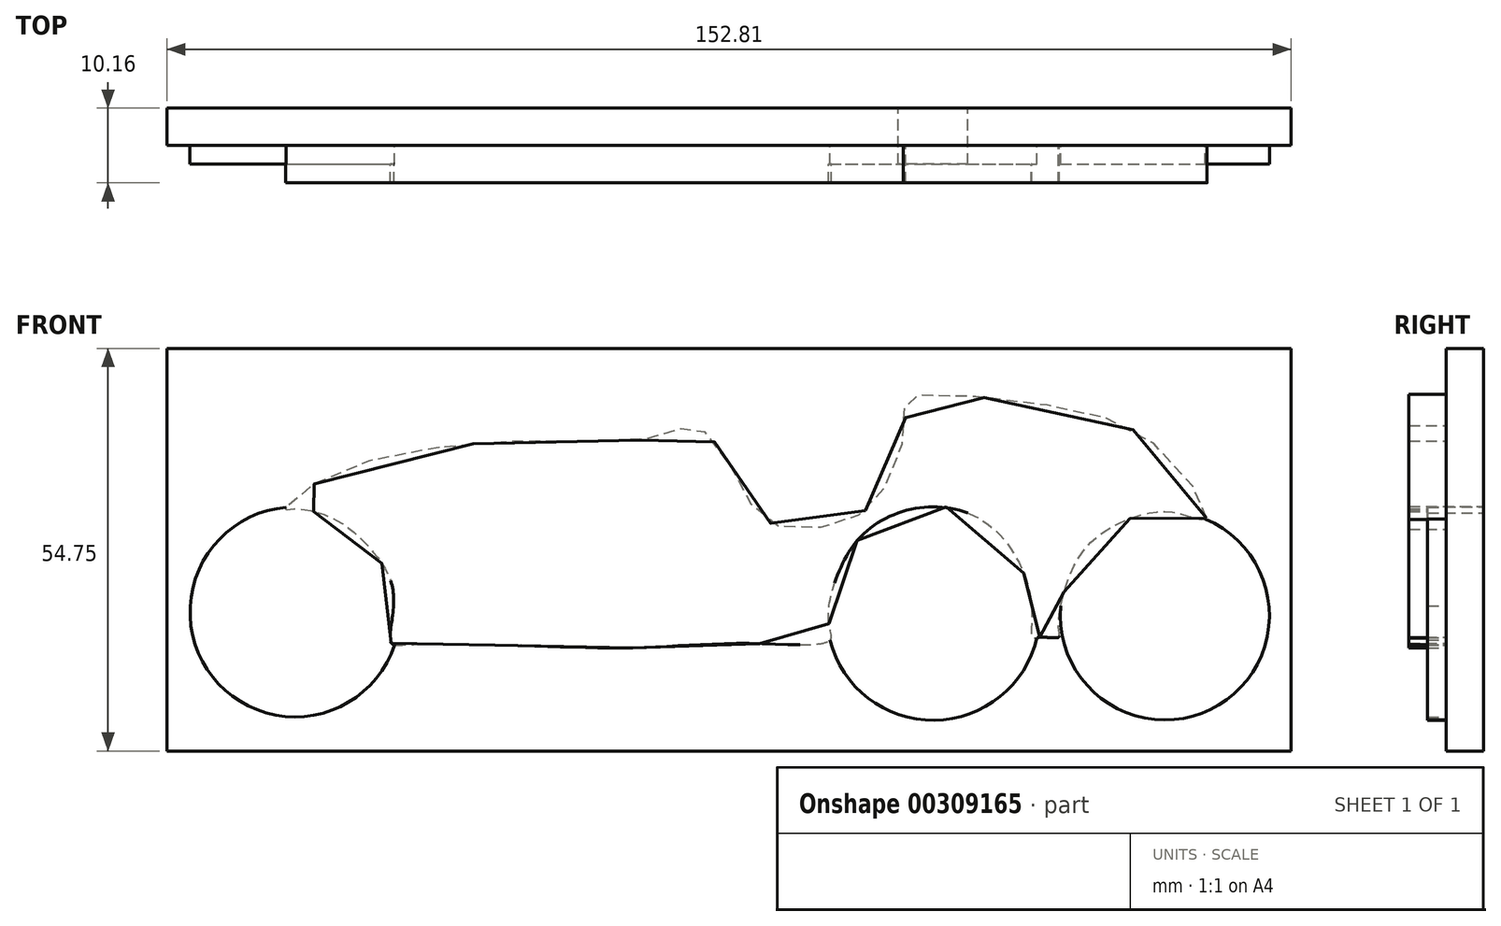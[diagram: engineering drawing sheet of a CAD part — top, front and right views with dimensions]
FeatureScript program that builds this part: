
annotation { "Feature Type Name" : "Feature", "Feature Type Description" : "" }
export const myFeature = defineFeature(function(context is Context, id is Id, definition is map)
    precondition{}
    {
        {
            var Q0;
            Q0=qCreatedBy(makeId("Front.planeOp"),FACE);
            var sketch = newSketch(context, id + "F0", { "sketchPlane" : qUnion([Q0])});
            skFitSpline(sketch, "E0", {"points": [v(91.57, -9.24) * mm, v(85.46, 0) * mm, v(68.77, 6.28) * mm, v(50.67, 6.98) * mm, v(50.67, 4.63) * mm, v(47.6, -5.48) * mm, v(41.73, -9.95) * mm, v(32.33, -9.95) * mm, v(27.86, -3.83) * mm, v(22.22, 3.22) * mm, v(18.22, 2.04) * mm, v(-1.62, 1.2) * mm, v(-28.2, -3.75) * mm, v(-33.55, -8) * mm, v(-32.54, -8) * mm, v(-27.09, -9.3) * mm, v(-21.67, -13.85) * mm, v(-18.88, -19.98) * mm, v(-19.29, -26.1) * mm, v(-17.52, -26.47) * mm, v(-2.12, -26.56) * mm, v(14.58, -26.84) * mm, v(29.22, -26.28) * mm, v(40.42, -25.81) * mm, v(40.25, -23.5) * mm, v(41.6, -16.58) * mm, v(46.02, -10.5) * mm, v(54.62, -7.63) * mm, v(63.21, -11.21) * mm, v(67.8, -21.06) * mm, v(67.9, -25.5) * mm, v(68.97, -25.44) * mm, v(71.49, -25.44) * mm, v(71.49, -24.23) * mm, v(74.15, -14.72) * mm, v(80.72, -9.47) * mm, v(87.4, -8.51) * mm, v(91.57, -9.24) * mm]});
            skSolve(sketch);
        }
        {
            var Q0;
            Q0=makeQuery(id+"F0.imprint","IMPRINT",FACE,{"disambiguationData":[TD([[makeQuery(id+"F0.imprint","IMPRINT",EDGE,{"derivedFrom":sQuery(id+"F0.wireOp",EDGE,"E0")}),1.0]])]});
            extrude(context, id + "F1", {"entities" : qUnion([Q0]), "depth" : 5.08 * mm});
        }
        {
            var Q0;
            Q0=qCreatedBy(makeId("Front.planeOp"),FACE);
            var sketch = newSketch(context, id + "F2", { "sketchPlane" : qUnion([Q0])});
            skCircle(sketch, "E1", {"center": v(-32.3, -21.99) * mm, "radius": 14.27 * mm});
            skCircle(sketch, "E2", {"center": v(54.43, -22.22) * mm, "radius": 14.5 * mm});
            skCircle(sketch, "E3", {"center": v(85.92, -22.47) * mm, "radius": 14.21 * mm});
            skSolve(sketch);
        }
        {
            var Q0;
            Q0=makeQuery(id+"F2.imprint","IMPRINT",FACE,{"disambiguationData":[TD([[makeQuery(id+"F2.imprint","IMPRINT",EDGE,{"derivedFrom":sQuery(id+"F2.wireOp",EDGE,"E1")}),1.0]])]});
            var Q1;
            Q1=makeQuery(id+"F2.imprint","IMPRINT",FACE,{"disambiguationData":[TD([[makeQuery(id+"F2.imprint","IMPRINT",EDGE,{"derivedFrom":sQuery(id+"F2.wireOp",EDGE,"E2")}),1.0]])]});
            var Q2;
            Q2=makeQuery(id+"F2.imprint","IMPRINT",FACE,{"disambiguationData":[TD([[makeQuery(id+"F2.imprint","IMPRINT",EDGE,{"derivedFrom":sQuery(id+"F2.wireOp",EDGE,"E3")}),1.0]])]});
            extrude(context, id + "F3", {"entities" : qUnion([Q0, Q1, Q2]), "operationType" : NewBodyOperationType.ADD, "depth" : 2.54 * mm});
        }
        {
            var Q0;
            Q0=makeQuery(id+"F3.boolean.opBoolean","MERGE",FACE,{"derivedFrom":[makeQuery(id+"F1.opExtrude","CAP_FACE",FACE,{"disambiguationData":[OSD([sQuery(id+"F0.wireOp",EDGE,"E0")])],"isStart":true}),makeQuery(id+"F3.opExtrude","CAP_FACE",FACE,{"disambiguationData":[OSD([sQuery(id+"F2.wireOp",EDGE,"E1")])],"isStart":true}),makeQuery(id+"F3.opExtrude","CAP_FACE",FACE,{"disambiguationData":[OSD([sQuery(id+"F2.wireOp",EDGE,"E2")])],"isStart":true}),makeQuery(id+"F3.opExtrude","CAP_FACE",FACE,{"disambiguationData":[OSD([sQuery(id+"F2.wireOp",EDGE,"E3")])],"isStart":true})]});
            var sketch = newSketch(context, id + "F4", { "sketchPlane" : qUnion([Q0])});
            skLineSegment(sketch, "E4.bottom", {"start": v(-103.1, 13.84) * mm, "end": v(49.7, 13.84) * mm});
            skLineSegment(sketch, "E4.top", {"start": v(-103.1, -40.9) * mm, "end": v(49.7, -40.9) * mm});
            skLineSegment(sketch, "E4.left", {"start": v(-103.1, 13.84) * mm, "end": v(-103.1, -40.9) * mm});
            skLineSegment(sketch, "E4.right", {"start": v(49.7, 13.84) * mm, "end": v(49.7, -40.9) * mm});
            skSolve(sketch);
        }
        {
            var Q0;
            Q0=makeQuery(id+"F4.imprint","IMPRINT",FACE,{"disambiguationData":[TD([[makeQuery(id+"F4.imprint","IMPRINT",EDGE,{"derivedFrom":sQuery(id+"F4.wireOp",EDGE,"E4.bottom")}),-1.0]])]});
            var Q1;
            {var subQ10=sQuery(id+"F2.wireOp",EDGE,"E3");Q1=makeQuery(id+"F4.imprint","IMPRINT",FACE,{"disambiguationData":[TD([[makeQuery(id+"F4.imprint","IMPRINT",EDGE,{"derivedFrom":makeQuery(id+"F3.opExtrude","CAP_EDGE",EDGE,{"disambiguationData":[OSD([subQ10])],"isStart":true})}),-1.0]])]});}
            extrude(context, id + "F5", {"entities" : qUnion([Q0, Q1]), "operationType" : NewBodyOperationType.ADD, "depth" : 5.08 * mm});
        }
    });
